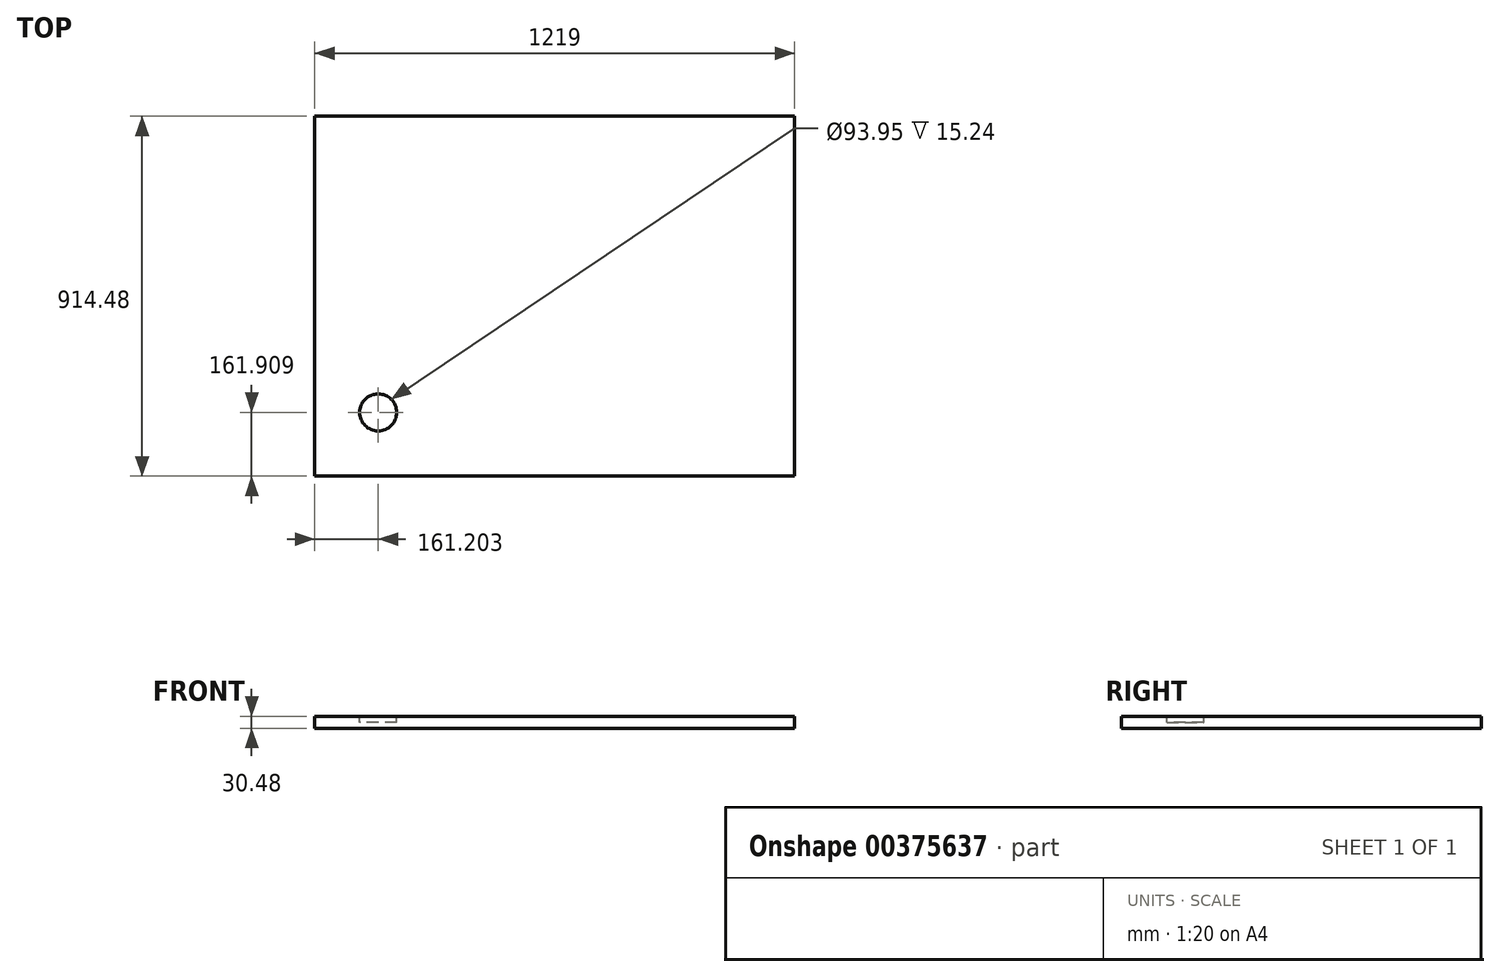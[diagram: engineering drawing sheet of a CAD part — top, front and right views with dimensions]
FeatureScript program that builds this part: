
annotation { "Feature Type Name" : "Feature", "Feature Type Description" : "" }
export const myFeature = defineFeature(function(context is Context, id is Id, definition is map)
    precondition{}
    {
        {
            var Q0;
            Q0=qCreatedBy(makeId("Top.planeOp"),FACE);
            var sketch = newSketch(context, id + "F0", { "sketchPlane" : qUnion([Q0])});
            skLineSegment(sketch, "E0.bottom", {"start": v(609.5, -457.24) * mm, "end": v(-609.5, -457.24) * mm});
            skLineSegment(sketch, "E0.top", {"start": v(609.5, 457.24) * mm, "end": v(-609.5, 457.24) * mm});
            skLineSegment(sketch, "E0.left", {"start": v(609.5, -457.24) * mm, "end": v(609.5, 457.24) * mm});
            skLineSegment(sketch, "E0.right", {"start": v(-609.5, -457.24) * mm, "end": v(-609.5, 457.24) * mm});
            skPoint(sketch, "E0.middle", {"position": v(0, 0) * mm});
            skSolve(sketch);
        }
        {
            var Q0;
            Q0=makeQuery(id+"F0.imprint","IMPRINT",FACE,{"disambiguationData":[TD([[makeQuery(id+"F0.imprint","IMPRINT",EDGE,{"derivedFrom":sQuery(id+"F0.wireOp",EDGE,"E0.bottom")}),-1.0]])]});
            extrude(context, id + "F1", {"entities" : qUnion([Q0]), "depth" : 30.48 * mm});
        }
        {
            var Q0;
            Q0=makeQuery(id+"F1.opExtrude","CAP_FACE",FACE,{"disambiguationData":[OSD([sQuery(id+"F0.wireOp",EDGE,"E0.bottom"),sQuery(id+"F0.wireOp",EDGE,"E0.top"),sQuery(id+"F0.wireOp",EDGE,"E0.left"),sQuery(id+"F0.wireOp",EDGE,"E0.right")])],"isStart":false});
            var sketch = newSketch(context, id + "F2", { "sketchPlane" : qUnion([Q0])});
            skSolve(sketch);
        }
        {
            var Q0;
            Q0=makeQuery(id+"F2.imprint","IMPRINT",FACE,{"disambiguationData":[TD([[makeQuery(id+"F2.imprint","IMPRINT",EDGE,{"derivedFrom":makeQuery(id+"F1.opExtrude","CAP_EDGE",EDGE,{"disambiguationData":[OSD([sQuery(id+"F0.wireOp",EDGE,"E0.bottom")])],"isStart":false})}),-1.0]])]});
            var sketch = newSketch(context, id + "F3", { "sketchPlane" : qUnion([Q0])});
            skCircle(sketch, "E1", {"center": v(-448.3, -295.33) * mm, "radius": 46.97 * mm});
            skSolve(sketch);
        }
        {
            var Q0;
            Q0=makeQuery(id+"F3.imprint","IMPRINT",FACE,{"disambiguationData":[TD([[makeQuery(id+"F3.imprint","IMPRINT",EDGE,{"derivedFrom":sQuery(id+"F3.wireOp",EDGE,"E1")}),1.0]])]});
            extrude(context, id + "F4", {"entities" : qUnion([Q0]), "operationType" : NewBodyOperationType.REMOVE, "oppositeDirection" : true, "depth" : 15.24 * mm});
        }
    });
